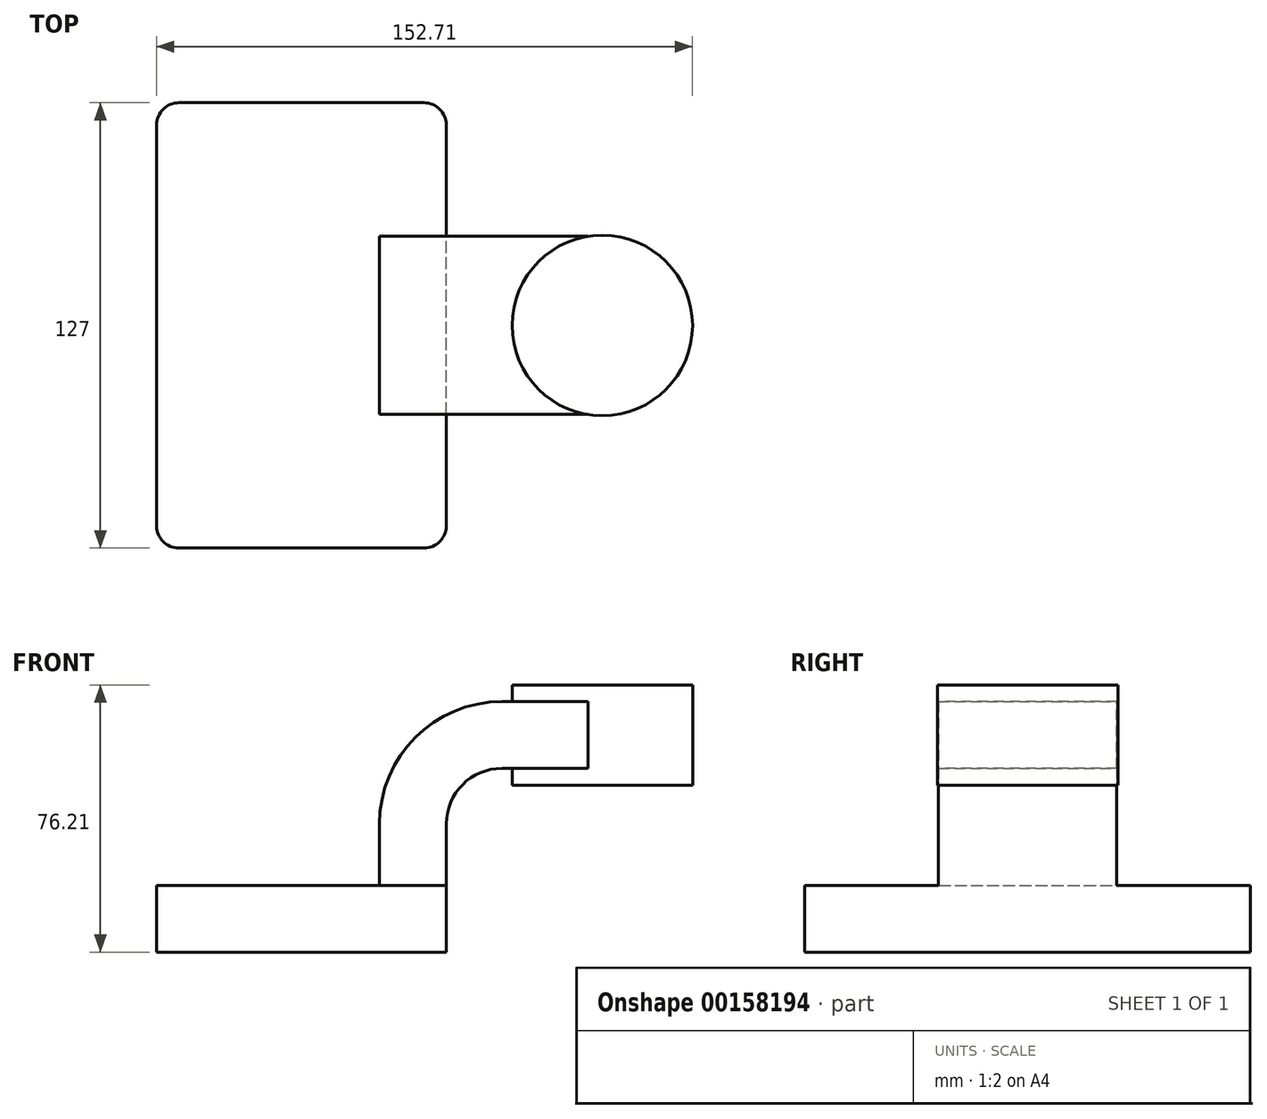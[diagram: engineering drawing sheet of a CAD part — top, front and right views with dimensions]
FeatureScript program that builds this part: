
annotation { "Feature Type Name" : "Feature", "Feature Type Description" : "" }
export const myFeature = defineFeature(function(context is Context, id is Id, definition is map)
    precondition{}
    {
        {
            var Q0;
            Q0=qCreatedBy(makeId("Front.planeOp"),FACE);
            var sketch = newSketch(context, id + "F0", { "sketchPlane" : qUnion([Q0])});
            skLineSegment(sketch, "E0.bottom", {"start": v(-41.28, 9.52) * mm, "end": v(41.28, 9.53) * mm});
            skLineSegment(sketch, "E0.top", {"start": v(-41.28, -9.53) * mm, "end": v(41.28, -9.53) * mm});
            skLineSegment(sketch, "E0.left", {"start": v(-41.28, 9.52) * mm, "end": v(-41.28, -9.53) * mm});
            skLineSegment(sketch, "E0.right", {"start": v(41.28, 9.53) * mm, "end": v(41.28, -9.52) * mm});
            skPoint(sketch, "E0.middle", {"position": v(0, 0) * mm});
            skLineSegment(sketch, "E1.bottom", {"start": v(111.44, 38.1) * mm, "end": v(59.06, 38.1) * mm});
            skLineSegment(sketch, "E1.top", {"start": v(111.44, 66.68) * mm, "end": v(59.06, 66.68) * mm});
            skLineSegment(sketch, "E1.left", {"start": v(111.44, 38.1) * mm, "end": v(111.44, 66.68) * mm});
            skLineSegment(sketch, "E1.right", {"start": v(59.06, 38.1) * mm, "end": v(59.06, 66.68) * mm});
            skPoint(sketch, "E1.middle", {"position": v(85.25, 52.39) * mm});
            skLineSegment(sketch, "E2", {"start": v(41.27, 9.53) * mm, "end": v(41.27, 27) * mm});
            skArc(sketch, "E3", {"start": v(41.27, 27) * mm, "mid": v(45.92, 38.23) * mm, "end": v(57.15, 42.88) * mm});
            skLineSegment(sketch, "E4", {"start": v(57.15, 42.88) * mm, "end": v(85.72, 42.88) * mm});
            skLineSegment(sketch, "E5.0", {"start": v(57.15, 61.93) * mm, "end": v(85.72, 61.93) * mm});
            skArc(sketch, "E5.1", {"start": v(22.22, 27) * mm, "mid": v(32.45, 51.7) * mm, "end": v(57.15, 61.93) * mm});
            skLineSegment(sketch, "E5.2", {"start": v(22.22, 9.53) * mm, "end": v(22.22, 27) * mm});
            skLineSegment(sketch, "E6", {"start": v(85.72, 66.68) * mm, "end": v(85.72, 38.1) * mm});
            skPoint(sketch, "E6.endSnap0", {"position": v(85.25, 38.1) * mm});
            skFitSpline(sketch, "E7", {"points": [v(-41.28, 9.52) * mm, v(57.15, 61.93) * mm], "startDerivative": vector(0.03, 81.47) * mm, "endDerivative": vector(123.02, -0.53) * mm});
            skSolve(sketch);
        }
        {
            var Q0;
            Q0=makeQuery(id+"F0.imprint","IMPRINT",FACE,{"disambiguationData":[TD([[makeQuery(id+"F0.imprint","IMPRINT",EDGE,{"derivedFrom":sQuery(id+"F0.wireOp",EDGE,"E0.top")}),1.0]])]});
            extrude(context, id + "F1", {"entities" : qUnion([Q0]), "endBound" : BoundingType.SYMMETRIC, "depth" : 127 * mm});
        }
        {
            var Q0;
            {var subQ1=sQuery(id+"F0.wireOp",EDGE,"E2");Q0=makeQuery(id+"F0.imprint","IMPRINT",FACE,{"disambiguationData":[TD([[makeQuery(id+"F0.imprint","IMPRINT",EDGE,{"derivedFrom":subQ1}),1.0]])]});}
            var Q1;
            {var subQ0=sQuery(id+"F0.wireOp",EDGE,"E4");var subQ1=sQuery(id+"F0.wireOp",EDGE,"E1.right");var subQ2=makeQuery(id+"F0.imprint","INTERSECT",VERTEX,{"derivedFrom":[subQ1,subQ0]});Q1=makeQuery(id+"F0.imprint","IMPRINT",FACE,{"disambiguationData":[TD([[makeQuery(id+"F0.imprint","IMPRINT",EDGE,{"disambiguationData":[TD([[subQ2,-1.0]])],"derivedFrom":subQ1}),-1.0]])]});}
            extrude(context, id + "F2", {"entities" : qUnion([Q0, Q1]), "operationType" : NewBodyOperationType.ADD, "endBound" : BoundingType.SYMMETRIC, "depth" : 50.8 * mm});
        }
        {
            var Q0;
            Q0=makeQuery(id+"F0.imprint","IMPRINT",FACE,{"disambiguationData":[TD([[makeQuery(id+"F0.imprint","IMPRINT",EDGE,{"derivedFrom":sQuery(id+"F0.wireOp",EDGE,"E5.1")}),1.0]])]});
            extrude(context, id + "F3", {"entities" : qUnion([Q0]), "operationType" : NewBodyOperationType.ADD, "endBound" : BoundingType.SYMMETRIC, "depth" : 15.88 * mm});
        }
        {
            var Q0;
            {var subQ0=sQuery(id+"F0.wireOp",EDGE,"E1.left");Q0=makeQuery(id+"F0.imprint","IMPRINT",FACE,{"disambiguationData":[TD([[makeQuery(id+"F0.imprint","IMPRINT",EDGE,{"derivedFrom":subQ0}),1.0]])]});}
            var Q1;
            Q1=sQuery(id+"F0.wireOp",EDGE,"E6");
            revolve(context, id + "F4", {"operationType" : NewBodyOperationType.ADD, "entities" : qUnion([Q0]), "axis" : qUnion([Q1]), "revolveType" : RevolveType.FULL});
        }
        {
            var Q0;
            Q0=makeQuery(id+"F1.opExtrude","CAP_EDGE",EDGE,{"disambiguationData":[OSD([sQuery(id+"F0.wireOp",EDGE,"E0.right")])],"isStart":false});
            var Q1;
            Q1=makeQuery(id+"F1.opExtrude","CAP_EDGE",EDGE,{"disambiguationData":[OSD([sQuery(id+"F0.wireOp",EDGE,"E0.right")])],"isStart":true});
            var Q2;
            Q2=makeQuery(id+"F1.opExtrude","CAP_EDGE",EDGE,{"disambiguationData":[OSD([sQuery(id+"F0.wireOp",EDGE,"E0.left")])],"isStart":false});
            var Q3;
            Q3=makeQuery(id+"F1.opExtrude","CAP_EDGE",EDGE,{"disambiguationData":[OSD([sQuery(id+"F0.wireOp",EDGE,"E0.left")])],"isStart":true});
            fillet(context, id + "F5", {"entities" : qUnion([Q0, Q1, Q2, Q3]), "radius" : 6.35 * mm, "tangentPropagation" : true, "allowEdgeOverflow" : false});
        }
    });
